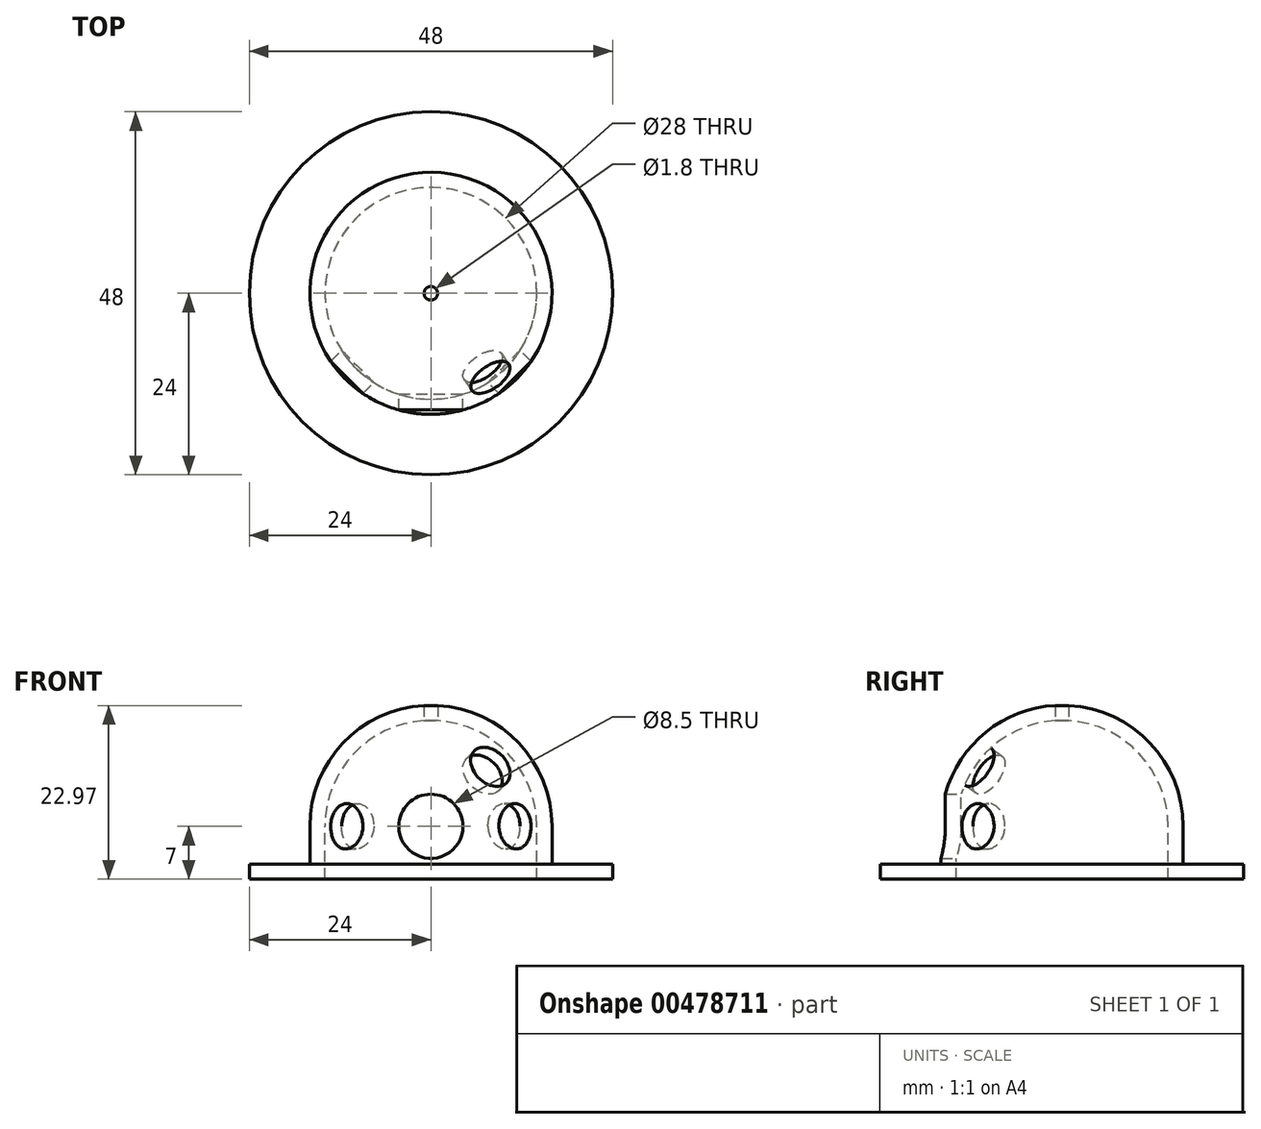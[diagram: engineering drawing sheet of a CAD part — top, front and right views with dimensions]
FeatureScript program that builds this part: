
annotation { "Feature Type Name" : "Feature", "Feature Type Description" : "" }
export const myFeature = defineFeature(function(context is Context, id is Id, definition is map)
    precondition{}
    {
        {
            var Q0;
            Q0=qCreatedBy(makeId("Front.planeOp"),FACE);
            var sketch = newSketch(context, id + "F0", { "sketchPlane" : qUnion([Q0])});
            skLineSegment(sketch, "E0", {"start": v(-14, -7) * mm, "end": v(-24, -7) * mm});
            skLineSegment(sketch, "E1", {"start": v(-24, -7) * mm, "end": v(-24, -5) * mm});
            skLineSegment(sketch, "E2", {"start": v(-24, -5) * mm, "end": v(-16, -5) * mm});
            skLineSegment(sketch, "E3", {"start": v(-16, -5) * mm, "end": v(-16, 0) * mm});
            skLineSegment(sketch, "E4", {"start": v(-14, -7) * mm, "end": v(-14, 0) * mm});
            skArc(sketch, "E5", {"start": v(0, 14) * mm, "mid": v(-9.9, 9.9) * mm, "end": v(-14, 0) * mm});
            skArc(sketch, "E6", {"start": v(0, 16) * mm, "mid": v(-11.31, 11.31) * mm, "end": v(-16, 0) * mm});
            skLineSegment(sketch, "E7", {"start": v(0, 16) * mm, "end": v(0, 14) * mm});
            skSolve(sketch);
        }
        {
            var Q0;
            Q0=qSketchRegion(id+"F0",true);
            var Q1;
            Q1=sQuery(id+"F0.wireOp",EDGE,"E7");
            revolve(context, id + "F1", {"entities" : qUnion([Q0]), "axis" : qUnion([Q1]), "revolveType" : RevolveType.FULL});
        }
        {
            var Q0;
            Q0=qCreatedBy(makeId("Front.planeOp"),FACE);
            var sketch = newSketch(context, id + "F2", { "sketchPlane" : qUnion([Q0])});
            skCircle(sketch, "E8", {"center": v(0, 0) * mm, "radius": 4.25 * mm});
            skSolve(sketch);
        }
        {
            var Q0;
            Q0=qSketchRegion(id+"F2",true);
            extrude(context, id + "F3", {"entities" : qUnion([Q0]), "operationType" : NewBodyOperationType.REMOVE, "depth" : 50 * mm});
        }
        {
            var Q0;
            Q0=qCreatedBy(makeId("Top.planeOp"),FACE);
            var sketch = newSketch(context, id + "F4", { "sketchPlane" : qUnion([Q0])});
            skLineSegment(sketch, "E9", {"start": v(-39.11, -39.11) * mm, "end": v(32.62, 32.62) * mm, "construction": true});
            skLineSegment(sketch, "E10", {"start": v(-37.35, 37.35) * mm, "end": v(42.98, -42.98) * mm, "construction": true});
            skSolve(sketch);
        }
        {
            var Q0;
            Q0=sQuery(id+"F4.wireOp",EDGE,"E10");
            cPlane(context, id + "F5", {"entities" : qUnion([Q0]), "cplaneType" : CPlaneType.LINE_ANGLE, "offset" : 25 * mm, "angle" : 90 * degree, "width" : 150 * mm, "height" : 150 * mm});
        }
        {
            var Q0;
            Q0=qCreatedBy(id+"F5.planeOp",FACE);
            var sketch = newSketch(context, id + "F6", { "sketchPlane" : qUnion([Q0])});
            skCircle(sketch, "E11", {"center": v(0, 0) * mm, "radius": 3 * mm});
            skSolve(sketch);
        }
        {
            var Q0;
            Q0=qSketchRegion(id+"F6",true);
            extrude(context, id + "F7", {"entities" : qUnion([Q0]), "operationType" : NewBodyOperationType.REMOVE, "oppositeDirection" : true, "depth" : 25 * mm});
        }
        {
            var Q0;
            Q0=qCreatedBy(makeId("Front.planeOp"),FACE);
            var sketch = newSketch(context, id + "F8", { "sketchPlane" : qUnion([Q0])});
            skLineSegment(sketch, "E12", {"start": v(0, 0) * mm, "end": v(30.29, 30.29) * mm, "construction": true});
            skLineSegment(sketch, "E13", {"start": v(0, 0) * mm, "end": v(-31.13, 31.13) * mm, "construction": true});
            skSolve(sketch);
        }
        {
            var Q0;
            Q0=sQuery(id+"F8.wireOp",EDGE,"E12");
            cPlane(context, id + "F9", {"entities" : qUnion([Q0]), "cplaneType" : CPlaneType.LINE_ANGLE, "offset" : 25 * mm, "angle" : 90 * degree, "width" : 150 * mm, "height" : 150 * mm});
        }
        {
            var Q0;
            Q0=qCreatedBy(id+"F9.planeOp",FACE);
            var sketch = newSketch(context, id + "F10", { "sketchPlane" : qUnion([Q0])});
            skLineSegment(sketch, "E14", {"start": v(0, 0) * mm, "end": v(19.81, 19.81) * mm, "construction": true});
            skLineSegment(sketch, "E15", {"start": v(16.68, 16.68) * mm, "end": v(14.56, 18.8) * mm});
            skLineSegment(sketch, "E16", {"start": v(14.56, 18.8) * mm, "end": v(1.88, 6.12) * mm});
            skLineSegment(sketch, "E17", {"start": v(1.88, 6.12) * mm, "end": v(4, 4) * mm});
            skLineSegment(sketch, "E18", {"start": v(4, 4) * mm, "end": v(16.68, 16.68) * mm});
            skSolve(sketch);
        }
        {
            var Q0;
            Q0=qSketchRegion(id+"F10",true);
            var Q1;
            Q1=sQuery(id+"F10.wireOp",EDGE,"E18");
            revolve(context, id + "F11", {"operationType" : NewBodyOperationType.REMOVE, "entities" : qUnion([Q0]), "axis" : qUnion([Q1]), "revolveType" : RevolveType.FULL, "oppositeDirection" : true});
        }
        {
            var Q0;
            Q0=sQuery(id+"F4.wireOp",EDGE,"E9");
            cPlane(context, id + "F12", {"entities" : qUnion([Q0]), "cplaneType" : CPlaneType.LINE_ANGLE, "offset" : 25 * mm, "angle" : 90 * degree, "width" : 150 * mm, "height" : 150 * mm});
        }
        {
            var Q0;
            Q0=qCreatedBy(id+"F12.planeOp",FACE);
            var sketch = newSketch(context, id + "F13", { "sketchPlane" : qUnion([Q0])});
            skCircle(sketch, "E19", {"center": v(0, 0) * mm, "radius": 3 * mm});
            skSolve(sketch);
        }
        {
            var Q0;
            Q0=qSketchRegion(id+"F13",true);
            extrude(context, id + "F14", {"entities" : qUnion([Q0]), "operationType" : NewBodyOperationType.REMOVE, "depth" : 25 * mm});
        }
        {
            var Q0;
            Q0=sQuery(id+"F8.wireOp",EDGE,"E13");
            cPlane(context, id + "F15", {"entities" : qUnion([Q0]), "cplaneType" : CPlaneType.LINE_ANGLE, "offset" : 25 * mm, "angle" : 90 * degree, "width" : 150 * mm, "height" : 150 * mm});
        }
        {
            var Q0;
            Q0=qCreatedBy(makeId("Top.planeOp"),FACE);
            var sketch = newSketch(context, id + "F16", { "sketchPlane" : qUnion([Q0])});
            skCircle(sketch, "E20", {"center": v(0, 0) * mm, "radius": 0.9 * mm});
            skSolve(sketch);
        }
        {
            var Q0;
            Q0 = qSketchRegion(id + "F16", true);
            extrude(context, id + "F17", {"entities" : qUnion([Q0]), "operationType" : NewBodyOperationType.REMOVE, "depth" : 30.1 * mm});
        }
        {
            var Q0;
            Q0=qCreatedBy(makeId("Right.planeOp"),FACE);
            var sketch = newSketch(context, id + "F18", { "sketchPlane" : qUnion([Q0])});
            skLineSegment(sketch, "E21", {"start": v(-34.54, 0) * mm, "end": v(39.7, 0) * mm, "construction": true});
            skSolve(sketch);
        }
        {
            var Q0;
            Q0=qCreatedBy(makeId("Top.planeOp"),FACE);
            var sketch = newSketch(context, id + "F19", { "sketchPlane" : qUnion([Q0])});
            skLineSegment(sketch, "E22", {"start": v(0, 0) * mm, "end": v(0, -71.29) * mm, "construction": true});
            skSolve(sketch);
        }
    });
